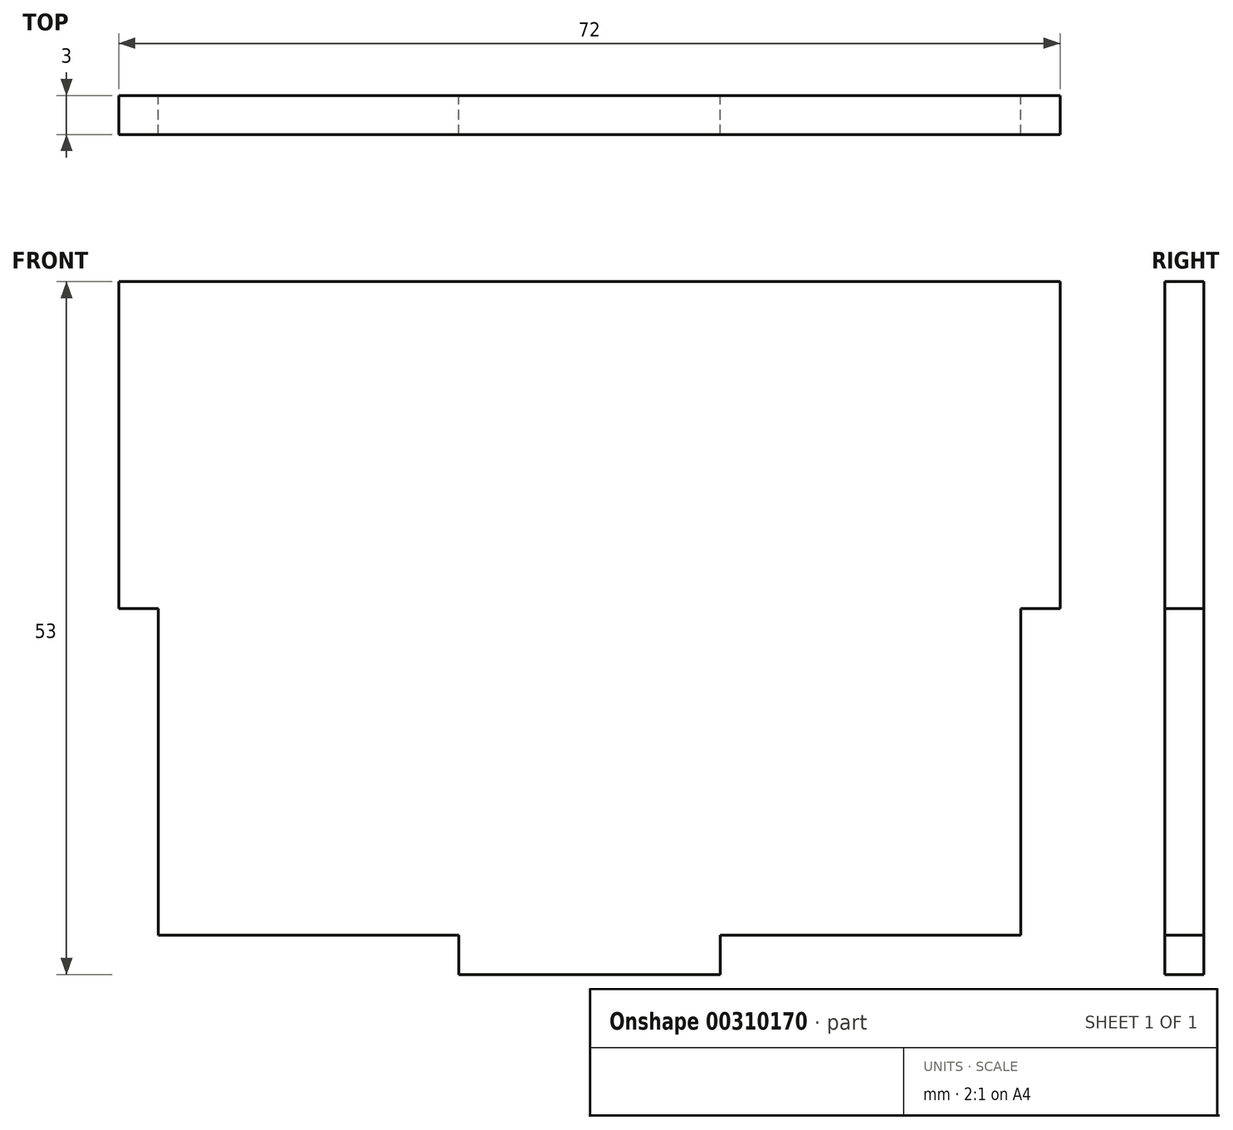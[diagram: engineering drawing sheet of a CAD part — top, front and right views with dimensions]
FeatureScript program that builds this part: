
annotation { "Feature Type Name" : "Feature", "Feature Type Description" : "" }
export const myFeature = defineFeature(function(context is Context, id is Id, definition is map)
    precondition{}
    {
        {
            var Q0;
            Q0=qCreatedBy(makeId("Front.planeOp"),FACE);
            var sketch = newSketch(context, id + "F0", { "sketchPlane" : qUnion([Q0])});
            skLineSegment(sketch, "E0.bottom", {"start": v(33, -25) * mm, "end": v(10, -25) * mm});
            skLineSegment(sketch, "E0.top", {"start": v(36, 25) * mm, "end": v(-36, 25) * mm});
            skLineSegment(sketch, "E0.left", {"start": v(36, 0) * mm, "end": v(36, 25) * mm});
            skLineSegment(sketch, "E0.right", {"start": v(-36, 0) * mm, "end": v(-36, 25) * mm});
            skPoint(sketch, "E0.middle", {"position": v(0, 0) * mm});
            skLineSegment(sketch, "E1.top", {"start": v(-36, 0) * mm, "end": v(-33, 0) * mm});
            skLineSegment(sketch, "E1.right", {"start": v(-33, -25) * mm, "end": v(-33, 0) * mm});
            skLineSegment(sketch, "E2.top", {"start": v(36, 0) * mm, "end": v(33, 0) * mm});
            skLineSegment(sketch, "E2.right", {"start": v(33, -25) * mm, "end": v(33, 0) * mm});
            skLineSegment(sketch, "E3.top", {"start": v(-10, -28) * mm, "end": v(10, -28) * mm});
            skLineSegment(sketch, "E3.left", {"start": v(-10, -25) * mm, "end": v(-10, -28) * mm});
            skLineSegment(sketch, "E3.right", {"start": v(10, -25) * mm, "end": v(10, -28) * mm});
            skLineSegment(sketch, "E4.trimOffspring", {"start": v(-10, -25) * mm, "end": v(-33, -25) * mm});
            skPoint(sketch, "E5.orphan", {"position": v(36, -25) * mm});
            skPoint(sketch, "E6.orphan", {"position": v(-36, -25) * mm});
            skSolve(sketch);
        }
        {
            var Q0;
            Q0=makeQuery(id+"F0.imprint","IMPRINT",FACE,{"disambiguationData":[TD([[makeQuery(id+"F0.imprint","IMPRINT",EDGE,{"derivedFrom":sQuery(id+"F0.wireOp",EDGE,"E0.bottom")}),-1.0]])]});
            extrude(context, id + "F1", {"entities" : qUnion([Q0]), "depth" : 3 * mm});
        }
    });
